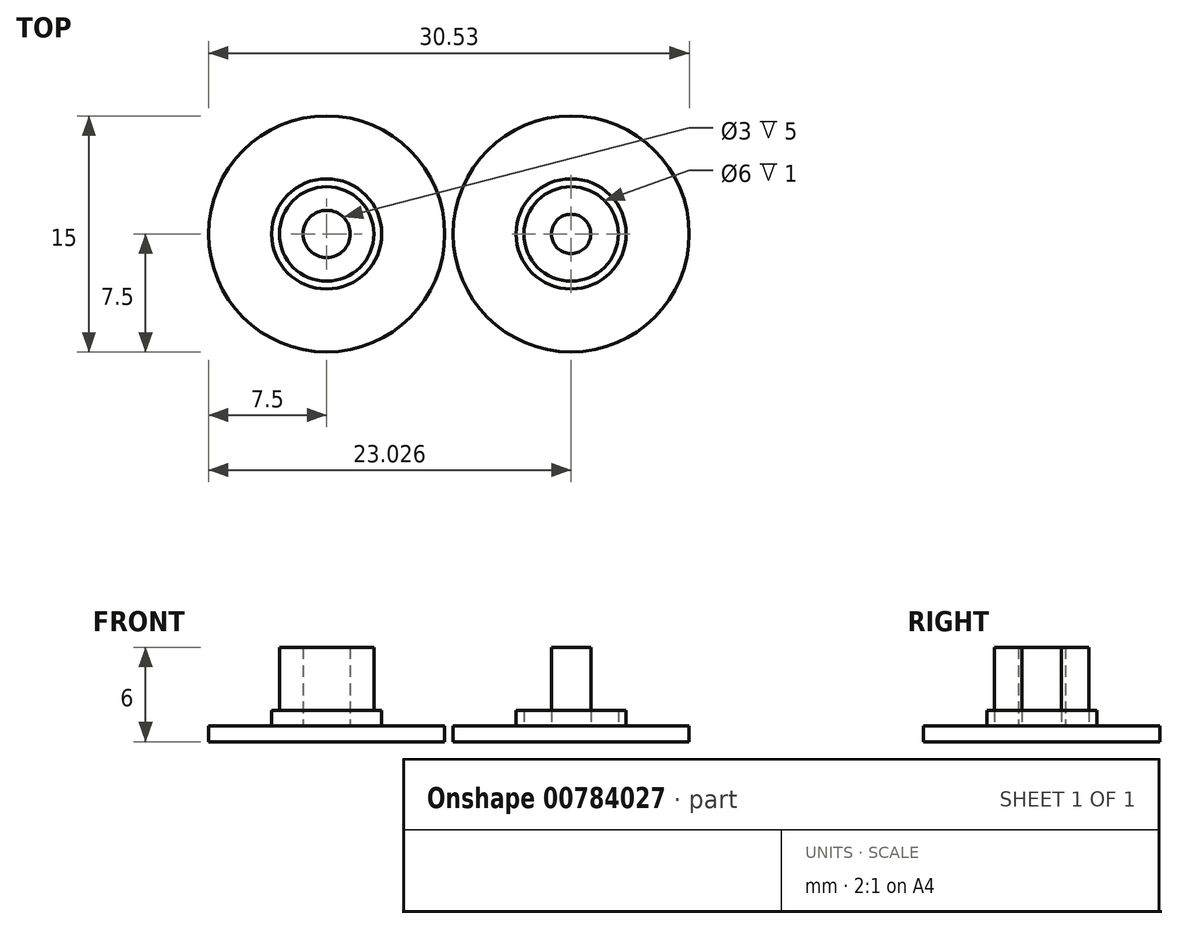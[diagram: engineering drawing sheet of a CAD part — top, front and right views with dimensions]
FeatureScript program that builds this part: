
annotation { "Feature Type Name" : "Feature", "Feature Type Description" : "" }
export const myFeature = defineFeature(function(context is Context, id is Id, definition is map)
    precondition{}
    {
        {
            var Q0;
            Q0=qCreatedBy(makeId("Top.planeOp"),FACE);
            var sketch = newSketch(context, id + "F0", { "sketchPlane" : qUnion([Q0])});
            skCircle(sketch, "E0", {"center": v(0, 0) * mm, "radius": 7.5 * mm});
            skCircle(sketch, "E1", {"center": v(0, 0) * mm, "radius": 3 * mm});
            skCircle(sketch, "E2", {"center": v(0, 0) * mm, "radius": 3.5 * mm});
            skCircle(sketch, "E3", {"center": v(0, 0) * mm, "radius": 1.5 * mm});
            skCircle(sketch, "E4", {"center": v(15.53, 0) * mm, "radius": 7.5 * mm});
            skCircle(sketch, "E5", {"center": v(15.53, 0) * mm, "radius": 3 * mm});
            skCircle(sketch, "E6", {"center": v(15.53, 0) * mm, "radius": 3.5 * mm});
            skCircle(sketch, "E7", {"center": v(15.53, 0) * mm, "radius": 1.25 * mm});
            skSolve(sketch);
        }
        {
            var Q0;
            Q0=makeQuery(id+"F0.imprint","IMPRINT",FACE,{"disambiguationData":[TD([[makeQuery(id+"F0.imprint","IMPRINT",EDGE,{"derivedFrom":sQuery(id+"F0.wireOp",EDGE,"E0")}),1.0]])]});
            var Q1;
            Q1=makeQuery(id+"F0.imprint","IMPRINT",FACE,{"disambiguationData":[TD([[makeQuery(id+"F0.imprint","IMPRINT",EDGE,{"derivedFrom":sQuery(id+"F0.wireOp",EDGE,"E4")}),1.0]])]});
            extrude(context, id + "F1", {"entities" : qUnion([Q0, Q1]), "depth" : 1 * mm, "offsetDistance" : 25 * mm});
        }
        {
            var Q0;
            Q0=makeQuery(id+"F0.imprint","IMPRINT",FACE,{"disambiguationData":[TD([[makeQuery(id+"F0.imprint","IMPRINT",EDGE,{"derivedFrom":sQuery(id+"F0.wireOp",EDGE,"E1")}),-1.0]])]});
            var Q1;
            Q1=makeQuery(id+"F0.imprint","IMPRINT",FACE,{"disambiguationData":[TD([[makeQuery(id+"F0.imprint","IMPRINT",EDGE,{"derivedFrom":sQuery(id+"F0.wireOp",EDGE,"E5")}),-1.0]])]});
            extrude(context, id + "F2", {"entities" : qUnion([Q0, Q1]), "operationType" : NewBodyOperationType.ADD, "depth" : 2 * mm, "offsetDistance" : 25 * mm});
        }
        {
            var Q0;
            Q0=makeQuery(id+"F0.imprint","IMPRINT",FACE,{"disambiguationData":[TD([[makeQuery(id+"F0.imprint","IMPRINT",EDGE,{"derivedFrom":sQuery(id+"F0.wireOp",EDGE,"E1")}),1.0]])]});
            var Q1;
            Q1=makeQuery(id+"F0.imprint","IMPRINT",FACE,{"disambiguationData":[TD([[makeQuery(id+"F0.imprint","IMPRINT",EDGE,{"derivedFrom":sQuery(id+"F0.wireOp",EDGE,"E7")}),1.0]])]});
            extrude(context, id + "F3", {"entities" : qUnion([Q0, Q1]), "operationType" : NewBodyOperationType.ADD, "depth" : 6 * mm, "offsetDistance" : 25 * mm});
        }
        {
            var Q0;
            Q0=makeQuery(id+"F0.imprint","IMPRINT",FACE,{"disambiguationData":[TD([[makeQuery(id+"F0.imprint","IMPRINT",EDGE,{"derivedFrom":sQuery(id+"F0.wireOp",EDGE,"E3")}),1.0]])]});
            var Q1;
            Q1=makeQuery(id+"F0.imprint","IMPRINT",FACE,{"disambiguationData":[TD([[makeQuery(id+"F0.imprint","IMPRINT",EDGE,{"derivedFrom":sQuery(id+"F0.wireOp",EDGE,"E5")}),1.0]])]});
            extrude(context, id + "F4", {"entities" : qUnion([Q0, Q1]), "operationType" : NewBodyOperationType.ADD, "depth" : 1 * mm, "offsetDistance" : 25 * mm});
        }
    });
